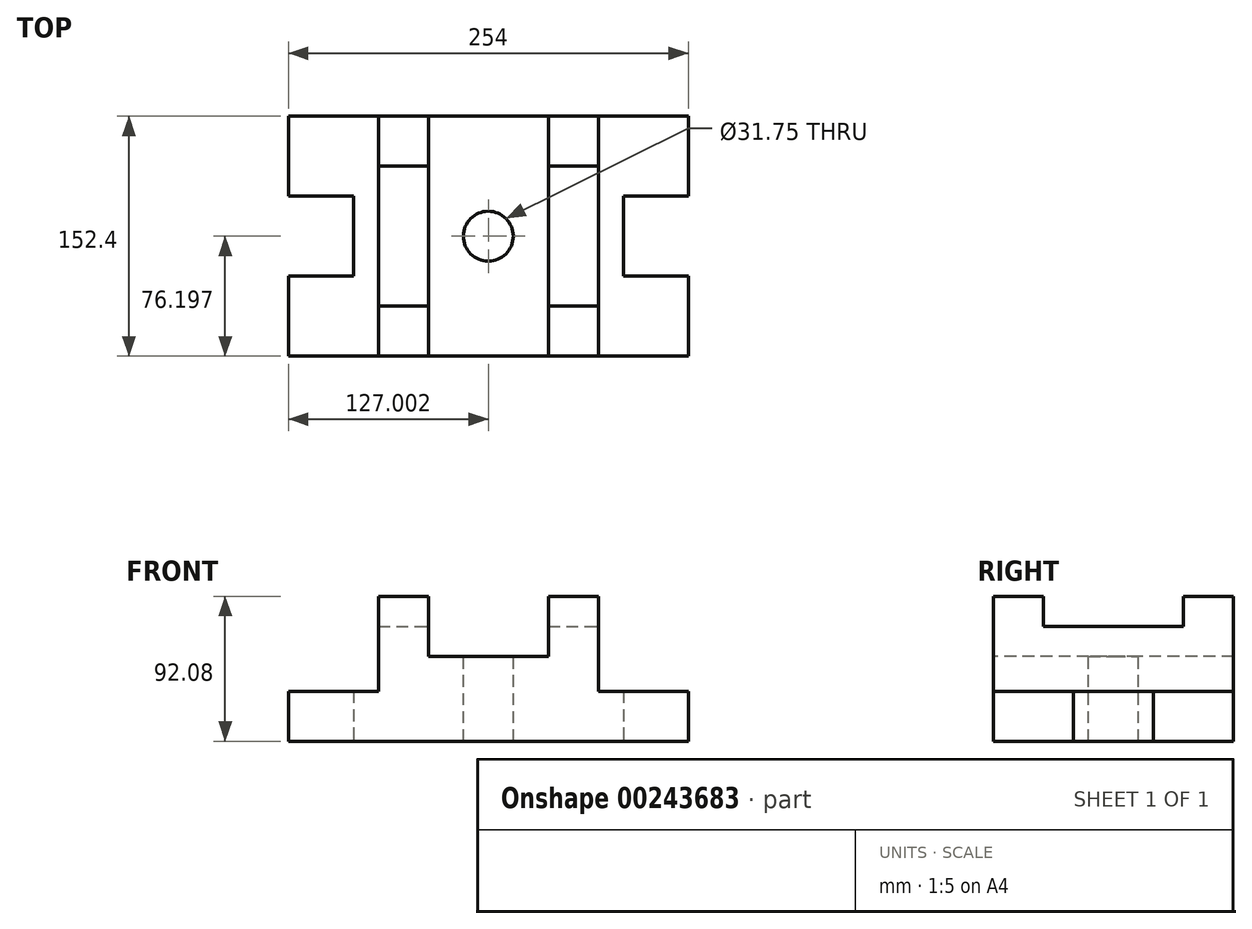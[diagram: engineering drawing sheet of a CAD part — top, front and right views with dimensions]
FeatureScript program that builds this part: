
annotation { "Feature Type Name" : "Feature", "Feature Type Description" : "" }
export const myFeature = defineFeature(function(context is Context, id is Id, definition is map)
    precondition{}
    {
        {
            var Q0;
            Q0=qCreatedBy(makeId("Top.planeOp"),FACE);
            var sketch = newSketch(context, id + "F0", { "sketchPlane" : qUnion([Q0])});
            skLineSegment(sketch, "E0.bottom", {"start": v(-131.45, 61.3) * mm, "end": v(122.55, 61.3) * mm});
            skLineSegment(sketch, "E0.top", {"start": v(-131.45, -91.1) * mm, "end": v(122.55, -91.1) * mm});
            skLineSegment(sketch, "E0.left", {"start": v(-131.45, 61.3) * mm, "end": v(-131.45, -91.1) * mm});
            skLineSegment(sketch, "E0.right", {"start": v(122.55, 61.3) * mm, "end": v(122.55, -91.1) * mm});
            skLineSegment(sketch, "E1", {"start": v(122.55, 10.5) * mm, "end": v(81.28, 10.5) * mm});
            skLineSegment(sketch, "E2", {"start": v(122.55, -40.3) * mm, "end": v(81.28, -40.3) * mm});
            skLineSegment(sketch, "E3", {"start": v(81.28, -40.3) * mm, "end": v(81.28, 10.5) * mm});
            skLineSegment(sketch, "E4.MirrorCS", {"start": v(-131.45, 10.5) * mm, "end": v(-90.17, 10.5) * mm});
            skLineSegment(sketch, "E5.MirrorCS", {"start": v(-90.17, -40.3) * mm, "end": v(-90.17, 10.5) * mm});
            skLineSegment(sketch, "E6.MirrorCS", {"start": v(-131.45, -40.3) * mm, "end": v(-90.17, -40.3) * mm});
            skSolve(sketch);
        }
        {
            var Q0;
            {var subQ4=sQuery(id+"F0.wireOp",EDGE,"E0.bottom");Q0=makeQuery(id+"F0.imprint","IMPRINT",FACE,{"disambiguationData":[TD([[makeQuery(id+"F0.imprint","IMPRINT",EDGE,{"derivedFrom":subQ4}),-1.0]])]});}
            extrude(context, id + "F1", {"entities" : qUnion([Q0]), "depth" : 31.75 * mm});
        }
        {
            var Q0;
            Q0=makeQuery(id+"F1.opExtrude","CAP_FACE",FACE,{"disambiguationData":[OSD([sQuery(id+"F0.wireOp",EDGE,"E0.bottom"),sQuery(id+"F0.wireOp",EDGE,"E0.top"),sQuery(id+"F0.wireOp",EDGE,"E0.left"),sQuery(id+"F0.wireOp",EDGE,"E0.right"),sQuery(id+"F0.wireOp",EDGE,"E1"),sQuery(id+"F0.wireOp",EDGE,"E2"),sQuery(id+"F0.wireOp",EDGE,"E3"),sQuery(id+"F0.wireOp",EDGE,"E4.MirrorCS"),sQuery(id+"F0.wireOp",EDGE,"E5.MirrorCS"),sQuery(id+"F0.wireOp",EDGE,"E6.MirrorCS")])],"isStart":false});
            var sketch = newSketch(context, id + "F2", { "sketchPlane" : qUnion([Q0])});
            skLineSegment(sketch, "E7.bottom", {"start": v(33.65, 61.3) * mm, "end": v(65.4, 61.3) * mm});
            skLineSegment(sketch, "E7.top", {"start": v(33.65, 29.55) * mm, "end": v(65.4, 29.55) * mm});
            skLineSegment(sketch, "E7.left", {"start": v(33.65, 61.3) * mm, "end": v(33.65, 29.55) * mm});
            skLineSegment(sketch, "E7.right", {"start": v(65.4, 61.3) * mm, "end": v(65.4, 29.55) * mm});
            skLineSegment(sketch, "E8.bottom", {"start": v(-74.3, -59.35) * mm, "end": v(-42.55, -59.35) * mm});
            skLineSegment(sketch, "E8.top", {"start": v(-74.3, -91.1) * mm, "end": v(-42.55, -91.1) * mm});
            skLineSegment(sketch, "E8.left", {"start": v(-74.3, -59.35) * mm, "end": v(-74.3, -91.1) * mm});
            skLineSegment(sketch, "E8.right", {"start": v(-42.55, -59.35) * mm, "end": v(-42.55, -91.1) * mm});
            skLineSegment(sketch, "E9.bottom", {"start": v(33.65, -59.35) * mm, "end": v(65.4, -59.35) * mm});
            skLineSegment(sketch, "E9.top", {"start": v(33.65, -91.1) * mm, "end": v(65.4, -91.1) * mm});
            skLineSegment(sketch, "E9.left", {"start": v(33.65, -59.35) * mm, "end": v(33.65, -91.1) * mm});
            skLineSegment(sketch, "E9.right", {"start": v(65.4, -59.35) * mm, "end": v(65.4, -91.1) * mm});
            skLineSegment(sketch, "E10.MirrorCS", {"start": v(-42.55, 61.3) * mm, "end": v(-42.55, 29.55) * mm});
            skLineSegment(sketch, "E11.MirrorCS", {"start": v(-74.3, 61.3) * mm, "end": v(-74.3, 29.55) * mm});
            skLineSegment(sketch, "E12.MirrorCS", {"start": v(-42.55, 29.55) * mm, "end": v(-74.3, 29.55) * mm});
            skLineSegment(sketch, "E13.MirrorCS", {"start": v(-42.55, 61.3) * mm, "end": v(-74.3, 61.3) * mm});
            skSolve(sketch);
        }
        {
            var Q0;
            {var subQ0=sQuery(id+"F2.wireOp",EDGE,"E7.bottom");Q0=makeQuery(id+"F2.imprint","IMPRINT",FACE,{"disambiguationData":[TD([[makeQuery(id+"F2.imprint","IMPRINT",EDGE,{"derivedFrom":subQ0}),-1.0]])]});}
            var Q1;
            {var subQ0=sQuery(id+"F2.wireOp",EDGE,"80132977-9fe7-45dd-9590-642a04d6ba4b0.MirrorCS");Q1=makeQuery(id+"F2.imprint","IMPRINT",FACE,{"disambiguationData":[TD([[makeQuery(id+"F2.imprint","IMPRINT",EDGE,{"derivedFrom":subQ0}),1.0]])]});}
            var Q2;
            Q2=makeQuery(id+"F2.imprint","IMPRINT",FACE,{"disambiguationData":[TD([[makeQuery(id+"F2.imprint","IMPRINT",EDGE,{"derivedFrom":sQuery(id+"F2.wireOp",EDGE,"E9.bottom")}),-1.0]])]});
            var Q3;
            Q3=makeQuery(id+"F2.imprint","IMPRINT",FACE,{"disambiguationData":[TD([[makeQuery(id+"F2.imprint","IMPRINT",EDGE,{"derivedFrom":sQuery(id+"F2.wireOp",EDGE,"E8.bottom")}),-1.0]])]});
            var Q4;
            {var subQ0=sQuery(id+"F2.wireOp",EDGE,"08ae3ff7-ca78-4247-afa2-712e871724ba0.MirrorCS");Q4=makeQuery(id+"F2.imprint","IMPRINT",FACE,{"disambiguationData":[TD([[makeQuery(id+"F2.imprint","IMPRINT",EDGE,{"derivedFrom":subQ0}),-1.0]])]});}
            var Q5;
            {var subQ0=sQuery(id+"F2.wireOp",EDGE,"E7.top");Q5=makeQuery(id+"F2.imprint","IMPRINT",FACE,{"disambiguationData":[TD([[makeQuery(id+"F2.imprint","IMPRINT",EDGE,{"derivedFrom":subQ0}),1.0]])]});}
            var Q6;
            {var subQ0=sQuery(id+"F2.wireOp",EDGE,"E12.MirrorCS");Q6=makeQuery(id+"F2.imprint","IMPRINT",FACE,{"disambiguationData":[TD([[makeQuery(id+"F2.imprint","IMPRINT",EDGE,{"derivedFrom":subQ0}),-1.0]])]});}
            extrude(context, id + "F3", {"entities" : qUnion([Q0, Q1, Q2, Q3, Q4, Q5, Q6]), "operationType" : NewBodyOperationType.ADD, "depth" : 60.32 * mm});
        }
        {
            var Q0;
            Q0=makeQuery(id+"F1.opExtrude","CAP_FACE",FACE,{"disambiguationData":[OSD([sQuery(id+"F0.wireOp",EDGE,"E0.bottom"),sQuery(id+"F0.wireOp",EDGE,"E0.top"),sQuery(id+"F0.wireOp",EDGE,"E0.left"),sQuery(id+"F0.wireOp",EDGE,"E0.right"),sQuery(id+"F0.wireOp",EDGE,"E1"),sQuery(id+"F0.wireOp",EDGE,"E2"),sQuery(id+"F0.wireOp",EDGE,"E3"),sQuery(id+"F0.wireOp",EDGE,"E4.MirrorCS"),sQuery(id+"F0.wireOp",EDGE,"E5.MirrorCS"),sQuery(id+"F0.wireOp",EDGE,"E6.MirrorCS")])],"isStart":false});
            var sketch = newSketch(context, id + "F4", { "sketchPlane" : qUnion([Q0])});
            skLineSegment(sketch, "E14.bottom", {"start": v(-42.55, 61.3) * mm, "end": v(33.65, 61.3) * mm});
            skLineSegment(sketch, "E14.top", {"start": v(-42.55, -91.1) * mm, "end": v(33.65, -91.1) * mm});
            skLineSegment(sketch, "E14.left", {"start": v(-42.55, 61.3) * mm, "end": v(-42.55, -91.1) * mm});
            skLineSegment(sketch, "E14.right", {"start": v(33.65, 61.3) * mm, "end": v(33.65, -91.1) * mm});
            skSolve(sketch);
        }
        {
            var Q0;
            Q0 = qSketchRegion(id + "F4", true);
            extrude(context, id + "F5", {"entities" : qUnion([Q0]), "operationType" : NewBodyOperationType.ADD, "depth" : 22.22 * mm});
        }
        {
            var Q0;
            {var subQ0=sQuery(id+"F0.wireOp",EDGE,"E6.MirrorCS");var subQ1=sQuery(id+"F0.wireOp",EDGE,"E4.MirrorCS");var subQ2=sQuery(id+"F0.wireOp",EDGE,"E0.bottom");var subQ3=sQuery(id+"F0.wireOp",EDGE,"E0.top");var subQ4=sQuery(id+"F0.wireOp",EDGE,"E0.left");var subQ5=sQuery(id+"F0.wireOp",EDGE,"E5.MirrorCS");Q0=makeQuery(id+"F5.boolean.opBoolean","SPLIT",FACE,{"disambiguationData":[TD([makeQuery(id+"F1.opExtrude","SWEPT_FACE",FACE,{"disambiguationData":[OSD([subQ1])]})])],"derivedFrom":makeQuery(id+"F1.opExtrude","CAP_FACE",FACE,{"disambiguationData":[OSD([subQ2,subQ3,subQ4,sQuery(id+"F0.wireOp",EDGE,"E0.right"),sQuery(id+"F0.wireOp",EDGE,"E1"),sQuery(id+"F0.wireOp",EDGE,"E2"),sQuery(id+"F0.wireOp",EDGE,"E3"),subQ1,subQ5,subQ0])],"isStart":false})});}
            var sketch = newSketch(context, id + "F6", { "sketchPlane" : qUnion([Q0])});
            skLineSegment(sketch, "E15.bottom", {"start": v(-74.3, 29.55) * mm, "end": v(-42.55, 29.55) * mm});
            skLineSegment(sketch, "E15.top", {"start": v(-74.3, -59.35) * mm, "end": v(-42.55, -59.35) * mm});
            skLineSegment(sketch, "E15.left", {"start": v(-74.3, 29.55) * mm, "end": v(-74.3, -59.35) * mm});
            skLineSegment(sketch, "E15.right", {"start": v(-42.55, 29.55) * mm, "end": v(-42.55, -59.35) * mm});
            skSolve(sketch);
        }
        {
            var Q0;
            Q0=makeQuery(id+"F6.imprint","IMPRINT",FACE,{"disambiguationData":[TD([[makeQuery(id+"F6.imprint","IMPRINT",EDGE,{"derivedFrom":sQuery(id+"F6.wireOp",EDGE,"E15.bottom")}),1.0]])]});
            extrude(context, id + "F7", {"entities" : qUnion([Q0]), "operationType" : NewBodyOperationType.ADD, "depth" : 41.27 * mm});
        }
        {
            var Q0;
            {var subQ2=sQuery(id+"F0.wireOp",EDGE,"E2");var subQ3=sQuery(id+"F0.wireOp",EDGE,"E1");var subQ4=sQuery(id+"F0.wireOp",EDGE,"E0.bottom");var subQ5=sQuery(id+"F0.wireOp",EDGE,"E3");var subQ6=sQuery(id+"F0.wireOp",EDGE,"E0.top");var subQ7=sQuery(id+"F0.wireOp",EDGE,"E0.right");Q0=makeQuery(id+"F5.boolean.opBoolean","SPLIT",FACE,{"disambiguationData":[TD([makeQuery(id+"F1.opExtrude","SWEPT_FACE",FACE,{"disambiguationData":[OSD([subQ3])]})])],"derivedFrom":makeQuery(id+"F1.opExtrude","CAP_FACE",FACE,{"disambiguationData":[OSD([subQ4,subQ6,sQuery(id+"F0.wireOp",EDGE,"E0.left"),subQ7,subQ3,subQ2,subQ5,sQuery(id+"F0.wireOp",EDGE,"E4.MirrorCS"),sQuery(id+"F0.wireOp",EDGE,"E5.MirrorCS"),sQuery(id+"F0.wireOp",EDGE,"E6.MirrorCS")])],"isStart":false})});}
            var sketch = newSketch(context, id + "F8", { "sketchPlane" : qUnion([Q0])});
            skLineSegment(sketch, "E16.bottom", {"start": v(33.65, 29.55) * mm, "end": v(65.4, 29.55) * mm});
            skLineSegment(sketch, "E16.top", {"start": v(33.65, -59.35) * mm, "end": v(65.4, -59.35) * mm});
            skLineSegment(sketch, "E16.left", {"start": v(33.65, 29.55) * mm, "end": v(33.65, -59.35) * mm});
            skLineSegment(sketch, "E16.right", {"start": v(65.4, 29.55) * mm, "end": v(65.4, -59.35) * mm});
            skSolve(sketch);
        }
        {
            var Q0;
            Q0=makeQuery(id+"F5.opExtrude","CAP_FACE",FACE,{"disambiguationData":[OSD([sQuery(id+"F4.wireOp",EDGE,"E14.bottom"),sQuery(id+"F4.wireOp",EDGE,"E14.top"),sQuery(id+"F4.wireOp",EDGE,"E14.left"),sQuery(id+"F4.wireOp",EDGE,"E14.right")])],"isStart":false});
            var sketch = newSketch(context, id + "F9", { "sketchPlane" : qUnion([Q0])});
            skCircle(sketch, "E17", {"center": v(-4.45, -14.9) * mm, "radius": 10.86 * mm});
            skSolve(sketch);
        }
        {
            var Q0;
            Q0=sQuery(id+"F9.wireOp",VERTEX,"E17.center");
            var Q1;
            Q1=makeQuery(id+"F1.opExtrude","SWEPT_BODY",BODY,{"disambiguationData":[OSD([sQuery(id+"F0.wireOp",EDGE,"E0.bottom"),sQuery(id+"F0.wireOp",EDGE,"E0.top"),sQuery(id+"F0.wireOp",EDGE,"E0.left"),sQuery(id+"F0.wireOp",EDGE,"E0.right"),sQuery(id+"F0.wireOp",EDGE,"E1"),sQuery(id+"F0.wireOp",EDGE,"E2"),sQuery(id+"F0.wireOp",EDGE,"E3"),sQuery(id+"F0.wireOp",EDGE,"E4.MirrorCS"),sQuery(id+"F0.wireOp",EDGE,"E5.MirrorCS"),sQuery(id+"F0.wireOp",EDGE,"E6.MirrorCS")])]});
            hole(context, id + "F10", {"style" : HoleStyle.SIMPLE, "endStyle" : HoleEndStyle.THROUGH, "holeDiameter" : 31.75 * mm, "tappedDepth" : 12.7 * mm, "tapClearance" : 3, "locations" : qUnion([Q0]), "scope" : qUnion([Q1])});
        }
        {
            var Q0;
            Q0=makeQuery(id+"F8.imprint","IMPRINT",FACE,{"disambiguationData":[TD([[makeQuery(id+"F8.imprint","IMPRINT",EDGE,{"derivedFrom":sQuery(id+"F8.wireOp",EDGE,"E16.bottom")}),-1.0]])]});
            extrude(context, id + "F11", {"entities" : qUnion([Q0]), "operationType" : NewBodyOperationType.ADD, "depth" : 41.27 * mm});
        }
    });
